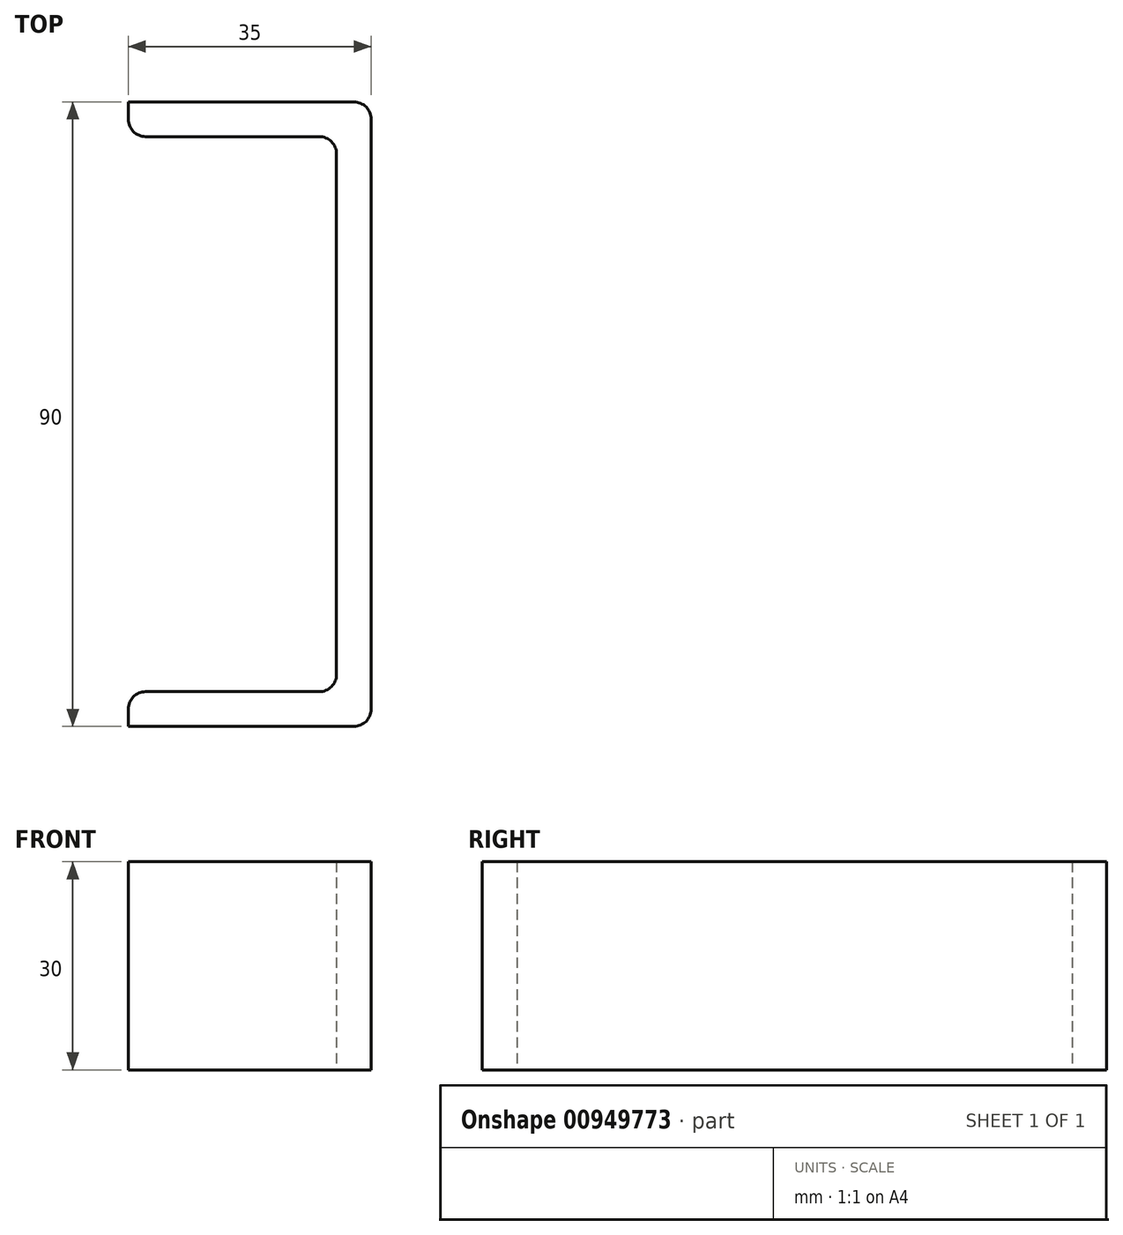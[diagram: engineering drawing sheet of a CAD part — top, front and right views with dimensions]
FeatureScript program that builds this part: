
annotation { "Feature Type Name" : "Feature", "Feature Type Description" : "" }
export const myFeature = defineFeature(function(context is Context, id is Id, definition is map)
    precondition{}
    {
        {
            var Q0;
            Q0=qCreatedBy(makeId("Top.planeOp"),FACE);
            var sketch = newSketch(context, id + "F0", { "sketchPlane" : qUnion([Q0])});
            skLineSegment(sketch, "E0", {"start": v(0, 37.93) * mm, "end": v(0, -47.07) * mm});
            skLineSegment(sketch, "E1", {"start": v(-2.5, 40.43) * mm, "end": v(-35, 40.43) * mm});
            skLineSegment(sketch, "E2", {"start": v(-2.5, -49.57) * mm, "end": v(-35, -49.57) * mm});
            skLineSegment(sketch, "E3", {"start": v(-35, 40.43) * mm, "end": v(-35, 37.93) * mm});
            skLineSegment(sketch, "E4", {"start": v(-32.5, 35.43) * mm, "end": v(-7.5, 35.43) * mm});
            skLineSegment(sketch, "E5", {"start": v(-5, 32.93) * mm, "end": v(-5, -42.07) * mm});
            skLineSegment(sketch, "E6", {"start": v(-7.5, -44.57) * mm, "end": v(-32.5, -44.57) * mm});
            skLineSegment(sketch, "E7", {"start": v(-35, -47.07) * mm, "end": v(-35, -49.57) * mm});
            skPoint(sketch, "E8.visualSharp", {"position": v(0, 40.43) * mm});
            skArc(sketch, "E8.filletArc", {"start": v(0, 37.93) * mm, "mid": v(-0.73, 39.7) * mm, "end": v(-2.5, 40.43) * mm});
            skPoint(sketch, "E9.visualSharp", {"position": v(0, -49.57) * mm});
            skArc(sketch, "E9.filletArc", {"start": v(-2.5, -49.57) * mm, "mid": v(-0.73, -48.84) * mm, "end": v(0, -47.07) * mm});
            skPoint(sketch, "E10.visualSharp", {"position": v(-5, -44.57) * mm});
            skArc(sketch, "E10.filletArc", {"start": v(-7.5, -44.57) * mm, "mid": v(-5.73, -43.84) * mm, "end": v(-5, -42.07) * mm});
            skPoint(sketch, "E11.visualSharp", {"position": v(-5, 35.43) * mm});
            skArc(sketch, "E11.filletArc", {"start": v(-5, 32.93) * mm, "mid": v(-5.73, 34.7) * mm, "end": v(-7.5, 35.43) * mm});
            skPoint(sketch, "E12.visualSharp", {"position": v(-35, 35.43) * mm});
            skArc(sketch, "E12.filletArc", {"start": v(-35, 37.93) * mm, "mid": v(-34.27, 36.16) * mm, "end": v(-32.5, 35.43) * mm});
            skPoint(sketch, "E13.visualSharp", {"position": v(-35, -44.57) * mm});
            skArc(sketch, "E13.filletArc", {"start": v(-32.5, -44.57) * mm, "mid": v(-34.27, -45.3) * mm, "end": v(-35, -47.07) * mm});
            skSolve(sketch);
        }
        {
            var Q0;
            Q0 = qSketchRegion(id + "F0", true);
            extrude(context, id + "F1", {"entities" : qUnion([Q0]), "depth" : 30 * mm, "offsetDistance" : 25 * mm});
        }
    });
